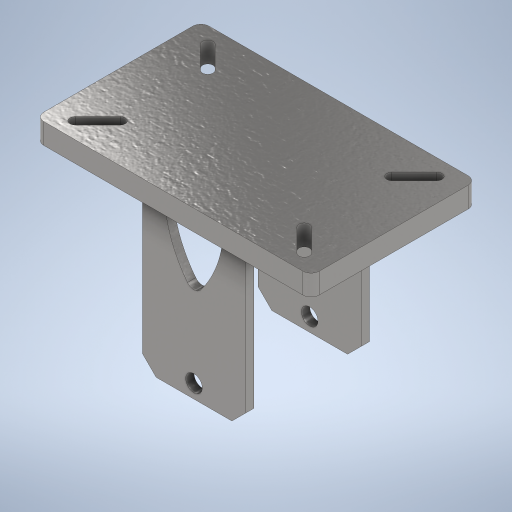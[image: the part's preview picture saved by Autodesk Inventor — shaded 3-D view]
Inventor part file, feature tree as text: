
AUTODESK INVENTOR PART (.ipt)
format: ipt  version: 2024 (Build 280153000, 153)  size: 392,192 bytes
history: native  units: mm
features: extrude x5, sketch x5, plane x2, mirror x2, fillet x2, chamfer x1
ambient origin geometry x8: Origin, YZ Plane, XZ Plane, XY Plane, X Axis, Y Axis, Z Axis, Center Point
bodies: Volumenkörper1 (feature_tree)
feature tree (17):
  extrude  "Extrusion1"  Depth=12.0mm
  extrude  "Extrusion2"  Depth=1.5mm
  plane  "Arbeitsebene1"
  mirror  "Spiegeln1"
  extrude  "Extrusion3"  Depth=0.749965mm
  chamfer  "Fasen1"  Angle=45.0deg  [1 undecoded]
  extrude  "Extrusion4"  Depth=1.5mm TaperAngle=0.0deg
  fillet  "Rundung1"  Radius=6.0mm
  extrude  "Extrusion5"  Depth=1.5mm
  plane  "Arbeitsebene2"
  mirror  "Spiegeln2"
  fillet  "Rundung2"  Radius=7.5mm
  sketch  "Skizze1"  dims[d0=20.0mm d1=12.0mm]
  sketch  "Skizze2"  dims[d2=1.5mm d3=0.0mm d7=15.0mm]
  sketch  "Skizze3"  dims[d8=7.5mm d9=0.749965mm]
  sketch  "Skizze4"  dims[d10=2.0mm]
  sketch  "Skizze5"  dims[d11=2.3mm d12=45.0deg d13=1.5mm d14=0.0mm d15=6.0mm d16=1.5mm d17=7.5mm d18=0.6mm d19=12.0mm d20=0.0mm d21=1.0mm d22=2.0mm d23=45.0deg d24=8.0mm d25=1.6mm d26=12.0mm d27=0.0mm d28=0.6mm d29=6.0mm d30=1.0mm d31=1.2mm d33=10.0mm d34=0.0mm d35=0.6mm]
note: 1 required parameter value undecoded (feature->parameter linkage not recoverable at this tier; creation-order binding heuristic only, values carry confidence <= 0.55)
